# Revit family: Overhead_Door_WD_Rapidshield_888
name_source: partatom
category: Doors
units: mm (PartAtom-declared; Revit-internal decimal feet)

## family parameters
Always vertical = Yes
Cut with Voids When Loaded = No
Host = Wall
OmniClass Number = 23.30.10.00
OmniClass Title = Doors
Room Calculation Point = No
Shared = No

## types (1)
- Overhead_Door_WD_Rapidshield_888
    Category = Doors
    Construction Details = https://www.arcat.com
    Cost = 0 $
    Door Height = 82
    Frame Finish = Finishes - WD - White
    Function = Interior
    Height = 21' - 0"
    Hood Material = Finishes - WD - White
    Keynote = 08 33 23.13
    Manufacturer = Wayne Dalton
    Manufacturer Website = https://www.wayne-dalton.com
    Model = Rapidshield
    Opening Height = 8' - 0"
    Opening Width = 8' - 0"
    Panel Material = Finishes - WD - White
    Product Data = https://www.arcat.com
    Product Properties = https://www.wayne-dalton.com
    Rough Height = 0' - 0"
    Rough Width = 0' - 0"
    Sales Information = https://www.wayne-dalton.com
    SpecWizard = https://www.arcat.com
    Specification = https://www.arcat.com
    Thickness = 0' - 0"
    URL = http://www.wayne-dalton.com
    Wall Closure = By host
    Width = 26' - 0"

## geometry (parser evidence)
native form markers: Sweep x7
no freeform markers — native parametric forms only
